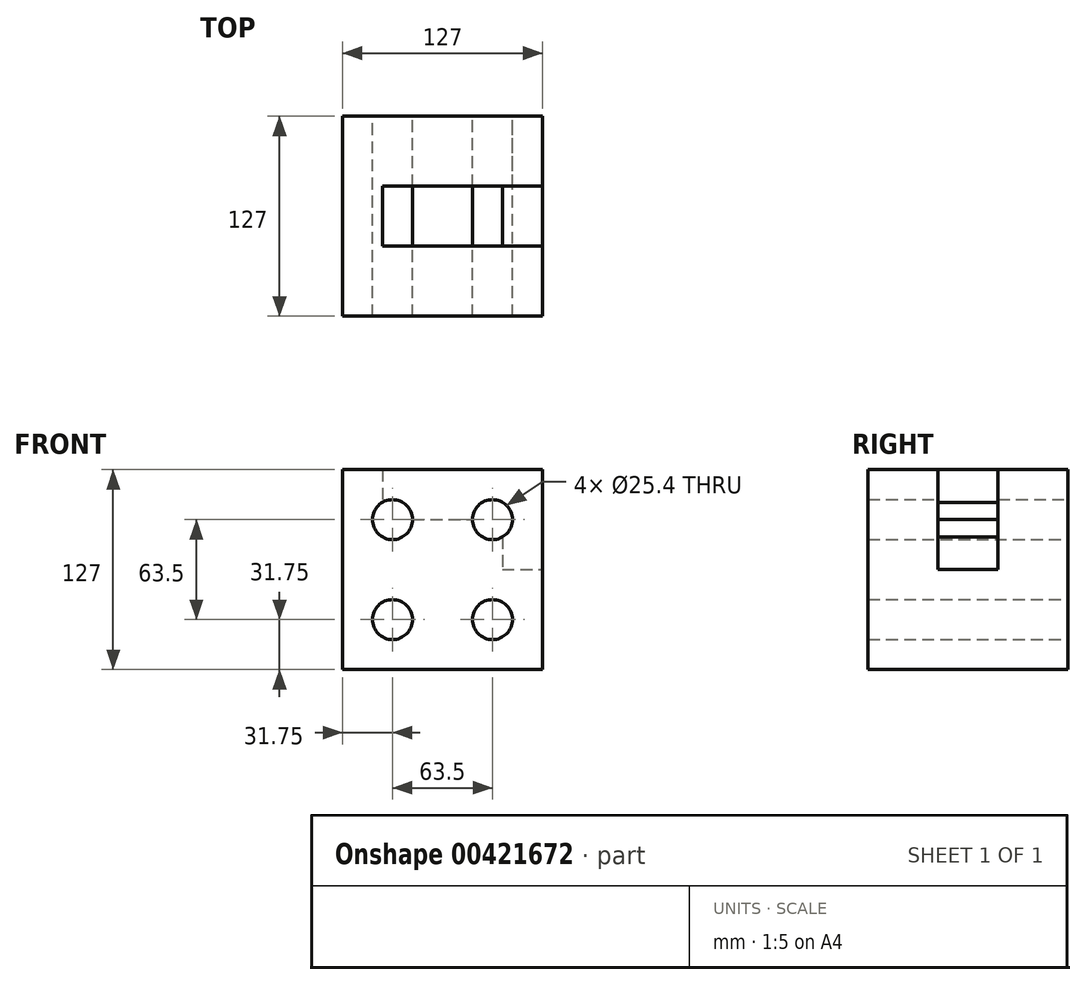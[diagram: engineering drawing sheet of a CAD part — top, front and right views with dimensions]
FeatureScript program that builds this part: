
annotation { "Feature Type Name" : "Feature", "Feature Type Description" : "" }
export const myFeature = defineFeature(function(context is Context, id is Id, definition is map)
    precondition{}
    {
        {
            var Q0;
            Q0=qCreatedBy(makeId("Front.planeOp"),FACE);
            var sketch = newSketch(context, id + "F0", { "sketchPlane" : qUnion([Q0])});
            skLineSegment(sketch, "E0.bottom", {"start": v(-63.5, 63.5) * mm, "end": v(63.5, 63.5) * mm});
            skLineSegment(sketch, "E0.top", {"start": v(-63.5, -63.5) * mm, "end": v(63.5, -63.5) * mm});
            skLineSegment(sketch, "E0.left", {"start": v(-63.5, 63.5) * mm, "end": v(-63.5, -63.5) * mm});
            skLineSegment(sketch, "E0.right", {"start": v(63.5, 63.5) * mm, "end": v(63.5, -63.5) * mm});
            skPoint(sketch, "E0.middle", {"position": v(0, 0) * mm});
            skCircle(sketch, "E1", {"center": v(-31.75, 31.75) * mm, "radius": 12.7 * mm});
            skCircle(sketch, "E2.0.1.0", {"center": v(-31.75, -31.75) * mm, "radius": 12.7 * mm});
            skCircle(sketch, "E2.1.0.0", {"center": v(31.75, 31.75) * mm, "radius": 12.7 * mm});
            skCircle(sketch, "E2.1.1.0", {"center": v(31.75, -31.75) * mm, "radius": 12.7 * mm});
            skLineSegment(sketch, "E2.direction1", {"start": v(-31.75, 31.75) * mm, "end": v(31.75, 31.75) * mm, "construction": true});
            skLineSegment(sketch, "E2.direction2", {"start": v(-31.75, 31.75) * mm, "end": v(-31.75, -31.75) * mm, "construction": true});
            skSolve(sketch);
        }
        {
            var Q0;
            Q0 = qSketchRegion(id + "F0", true);
            extrude(context, id + "F1", {"entities" : qUnion([Q0]), "depth" : 127 * mm});
        }
        {
            var Q0;
            Q0=makeQuery(id+"F1.opExtrude","SWEPT_FACE",FACE,{"disambiguationData":[OSD([sQuery(id+"F0.wireOp",EDGE,"E0.right")])]});
            var sketch = newSketch(context, id + "F2", { "sketchPlane" : qUnion([Q0])});
            skLineSegment(sketch, "E3.bottom", {"start": v(-82.55, 63.5) * mm, "end": v(-44.45, 63.5) * mm});
            skLineSegment(sketch, "E3.top", {"start": v(-82.55, 0) * mm, "end": v(-44.45, 0) * mm});
            skLineSegment(sketch, "E3.left", {"start": v(-82.55, 63.5) * mm, "end": v(-82.55, 0) * mm});
            skLineSegment(sketch, "E3.right", {"start": v(-44.45, 63.5) * mm, "end": v(-44.45, 0) * mm});
            skSolve(sketch);
        }
        {
            var Q0;
            Q0 = qSketchRegion(id + "F2", true);
            extrude(context, id + "F3", {"entities" : qUnion([Q0]), "operationType" : NewBodyOperationType.REMOVE, "oppositeDirection" : true, "depth" : 25.4 * mm});
        }
        {
            var Q0;
            {var subQ0=sQuery(id+"F2.wireOp",EDGE,"E3.right");var subQ1=sQuery(id+"F2.wireOp",EDGE,"E3.left");Q0=makeQuery(id+"F3.boolean.opBoolean","COPY",FACE,{"disambiguationData":[TD([makeQuery(id+"F1.opExtrude","SWEPT_FACE",FACE,{"disambiguationData":[OSD([sQuery(id+"F0.wireOp",EDGE,"E0.bottom")])]})])],"derivedFrom":makeQuery(id+"F3.opExtrude","CAP_FACE",FACE,{"disambiguationData":[OSD([sQuery(id+"F2.wireOp",EDGE,"E3.bottom"),sQuery(id+"F2.wireOp",EDGE,"E3.top"),subQ1,subQ0])],"isStart":false})});}
            var sketch = newSketch(context, id + "F4", { "sketchPlane" : qUnion([Q0])});
            skLineSegment(sketch, "E4.bottom", {"start": v(-82.55, 63.5) * mm, "end": v(-44.45, 63.5) * mm});
            skLineSegment(sketch, "E4.top", {"start": v(-82.55, 31.75) * mm, "end": v(-44.45, 31.75) * mm});
            skLineSegment(sketch, "E4.left", {"start": v(-82.55, 63.5) * mm, "end": v(-82.55, 31.75) * mm});
            skLineSegment(sketch, "E4.right", {"start": v(-44.45, 63.5) * mm, "end": v(-44.45, 31.75) * mm});
            skSolve(sketch);
        }
        {
            var Q0;
            Q0 = qSketchRegion(id + "F4", true);
            extrude(context, id + "F5", {"entities" : qUnion([Q0]), "operationType" : NewBodyOperationType.REMOVE, "oppositeDirection" : true, "depth" : 76.2 * mm});
        }
    });
